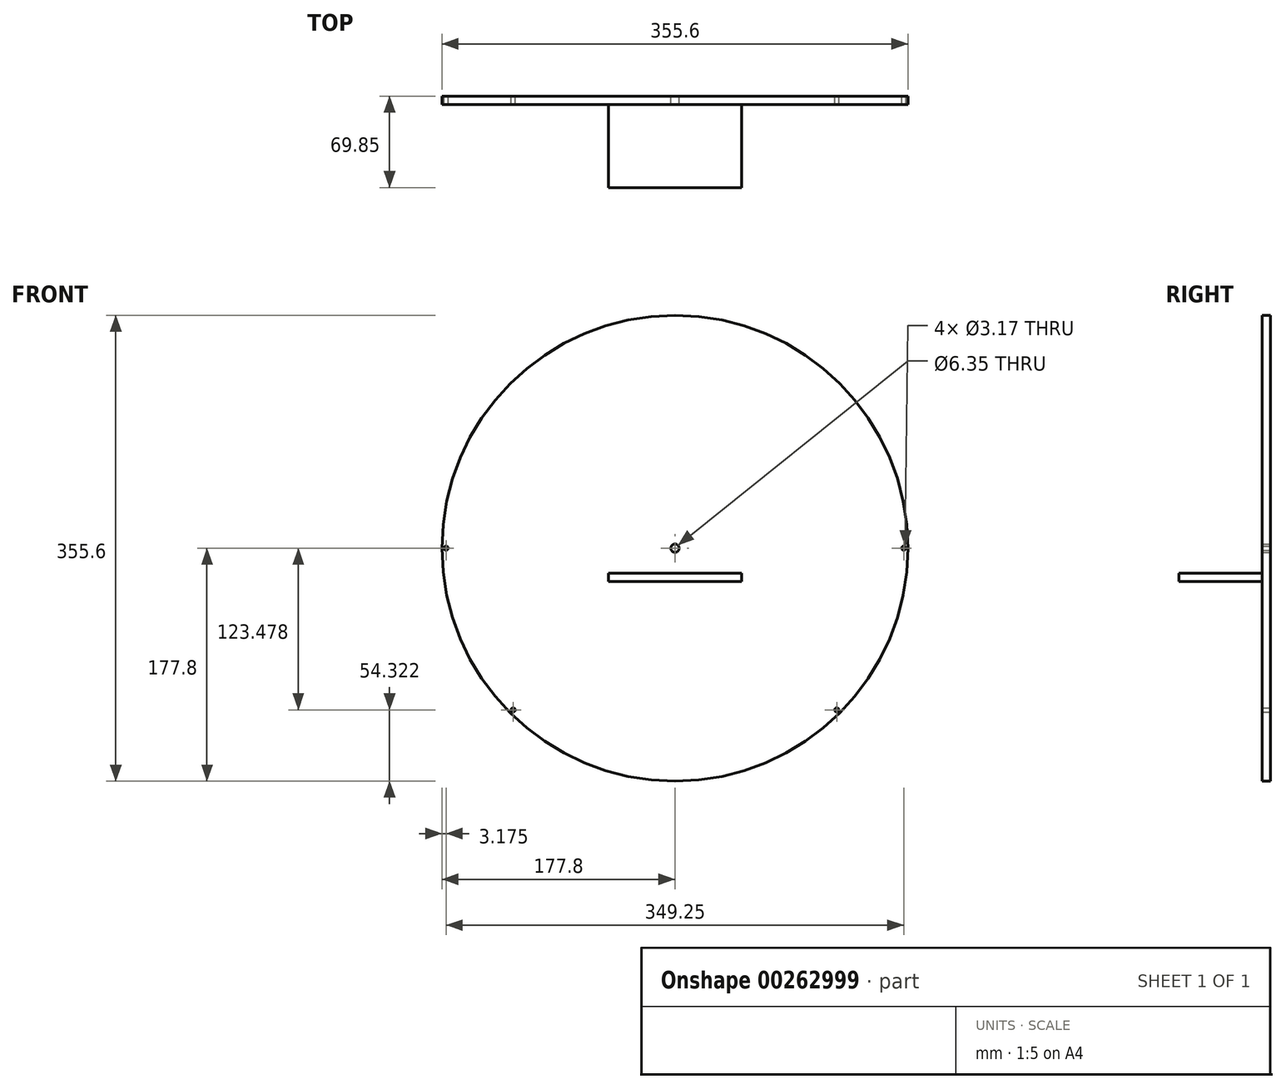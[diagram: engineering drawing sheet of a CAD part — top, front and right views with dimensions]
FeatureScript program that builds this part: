
annotation { "Feature Type Name" : "Feature", "Feature Type Description" : "" }
export const myFeature = defineFeature(function(context is Context, id is Id, definition is map)
    precondition{}
    {
        {
            var Q0;
            Q0=qCreatedBy(makeId("Front.planeOp"),FACE);
            var sketch = newSketch(context, id + "F0", { "sketchPlane" : qUnion([Q0])});
            skCircle(sketch, "E0", {"center": v(0, 0) * mm, "radius": 177.8 * mm});
            skCircle(sketch, "E1", {"center": v(0, 0) * mm, "radius": 3.18 * mm});
            skLineSegment(sketch, "E2.bottom", {"start": v(-50.8, -19.05) * mm, "end": v(50.8, -19.05) * mm});
            skLineSegment(sketch, "E2.top", {"start": v(-50.8, -25.4) * mm, "end": v(50.8, -25.4) * mm});
            skLineSegment(sketch, "E2.left", {"start": v(-50.8, -19.05) * mm, "end": v(-50.8, -25.4) * mm});
            skLineSegment(sketch, "E2.right", {"start": v(50.8, -19.05) * mm, "end": v(50.8, -25.4) * mm});
            skCircle(sketch, "E3", {"center": v(-174.62, 0) * mm, "radius": 1.59 * mm});
            skCircle(sketch, "E4", {"center": v(174.62, 0) * mm, "radius": 1.59 * mm});
            skPoint(sketch, "E5.centerSnap0", {"position": v(0, -25.4) * mm});
            skPoint(sketch, "E6.endSnap0", {"position": v(0, -19.05) * mm});
            skCircle(sketch, "E7", {"center": v(-123.48, -123.48) * mm, "radius": 1.59 * mm});
            skCircle(sketch, "E8", {"center": v(123.48, -123.48) * mm, "radius": 1.59 * mm});
            skSolve(sketch);
        }
        {
            var Q0;
            Q0=makeQuery(id+"F0.imprint","IMPRINT",FACE,{"disambiguationData":[TD([[makeQuery(id+"F0.imprint","IMPRINT",EDGE,{"derivedFrom":sQuery(id+"F0.wireOp",EDGE,"E0")}),1.0]])]});
            extrude(context, id + "F1", {"entities" : qUnion([Q0]), "depth" : 6.35 * mm});
        }
        {
            var Q0;
            Q0=makeQuery(id+"F0.imprint","IMPRINT",FACE,{"disambiguationData":[TD([[makeQuery(id+"F0.imprint","IMPRINT",EDGE,{"derivedFrom":sQuery(id+"F0.wireOp",EDGE,"E2.bottom")}),-1.0]])]});
            extrude(context, id + "F2", {"entities" : qUnion([Q0]), "operationType" : NewBodyOperationType.ADD, "depth" : 69.85 * mm});
        }
    });
